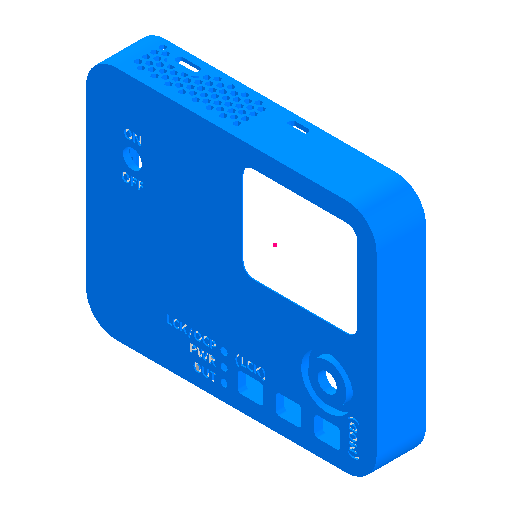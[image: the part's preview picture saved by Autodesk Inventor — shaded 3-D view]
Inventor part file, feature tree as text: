
AUTODESK INVENTOR PART (.ipt)
format: ipt  version: 2025 (Build 290162000, 162)  size: 3,334,144 bytes
history: native  units: mm
features: reference x98, sketch x43, extrude x31, other x19, fillet x6, chamfer x6, plane x4, sweep x2, mirror x2, shell x1, emboss x1, projected_geometry x1
ambient origin geometry x8: Origin, YZ Plane, XZ Plane, XY Plane, X Axis, Y Axis, Z Axis, Center Point
bodies: Solid1 (feature_tree)
feature tree (214):
  extrude  "Extrusion1"  Depth=3.0mm
  fillet  "Fillet1"  Radius=3.0mm
  shell  "Shell1"  Thickness=11.0mm
  extrude  "Extrusion_toggle"  Depth=0.3mm
  extrude  "Extrusion_encoder"  Depth=0.5mm
  extrude  "Extrusion_encoder_knob"  Depth=14.0mm
  extrude  "Extrusion_UI_BTNS"  Depth=2.6mm TaperAngle=0.0deg
  extrude  "Extrusion_Display"  Depth=2.0mm TaperAngle=0.0deg
  extrude  "Extrusion10"  Depth=10.0mm TaperAngle=0.0deg
  extrude  "Extrusion11"  Depth=3.3mm
  fillet  "Fillet4"  Radius=0.9mm
  plane  "Work Plane7"
  plane  "Work Plane8"
  extrude  "Extrusion17"  Depth=5.0mm
  extrude  "Extrusion18"  Depth=2.7mm TaperAngle=0.0deg
  sketch  "Sketch24"  dims[d107=0.25mm d108=0.0mm d109=0.3mm]
  extrude  "Extrusion19"  Depth=2.0mm
  extrude  "Extrusion20"  Depth=1.2mm
  extrude  "USB_C_1"  Depth=1.5mm TaperAngle=0.0deg
  extrude  "USB_C_2"  Depth=2.0mm TaperAngle=0.0deg
  extrude  "USB_Micro_B_1"  Depth=0.3mm
  extrude  "USB_Micro_B_2"  Depth=1.4mm TaperAngle=0.0deg
  extrude  "Venting_1"  Depth=0.25mm
  extrude  "Venting_2"  Depth=1.8mm TaperAngle=0.0deg
  sketch  "Sketch34"  dims[d142=40.0mm d144=3.0mm d145=10.0mm d147=10.0mm]
  extrude  "Extrusion27"  Depth=0.25mm
  chamfer  "Chamfer1"  Distance=1.4mm
  extrude  "Extrusion28"  Depth=7.0mm
  extrude  "Extrusion29"  TaperAngle=150.0deg  [1 undecoded]
  chamfer  "Chamfer3"  Distance=10.0mm
  extrude  "Extrusion30"  Depth=3.5mm
  extrude  "Display_hole_1"  Depth=0.3mm TaperAngle=45.0deg
  extrude  "Display_hole_2"  Depth=1.0mm
  fillet  "Fillet5"  Radius=1.0mm
  plane  "Work Plane9"
  plane  "Work Plane11"
  extrude  "Extrusion33"  Depth=0.7mm
  sweep  "Sweep2"
  chamfer  "Chamfer5"  Distance=1.8mm
  extrude  "Extrusion34"  Depth=0.7mm
  fillet  "Fillet7"  Radius=0.7mm
  chamfer  "Chamfer7"  Distance=2.5mm
  mirror  "Mirror1"
  mirror  "Mirror2"
  fillet  "Fillet8"  Radius=1.0mm
  chamfer  "Chamfer8"  Distance=1.8mm
  sketch  "Sketch44"  dims[d197=4.0mm d198=0.7mm d199=3.75mm d200=0.0mm d201=1.0mm d202=1.0mm]
  fillet  "Fillet9"  Radius=1.5mm
  sweep  "Sweep3"
  extrude  "Extrusion36"  Depth=0.4mm
  extrude  "Extrusion37"  Depth=0.4mm
  emboss  "Emboss1"
  extrude  "Extrusion38"  Depth=0.4mm
  chamfer  "Chamfer9"  Distance=4.0mm
  extrude  "Extrusion39"  Depth=0.4mm
  extrude  "Extrusion40"  Depth=0.4mm TaperAngle=0.0deg
  sketch  "Sketch1"  dims[d0=16.0mm d1=0.0mm d5=3.0mm d6=3.0mm d7=11.0mm]
  reference  "Reference1"
  reference  "Reference2"
  reference  "Reference3"
  reference  "Reference4"
  sketch  "Sketch3"  dims[d20=16.0mm d21=0.0mm d22=0.5mm]
  reference  "Reference53"
  sketch  "Sketch4"  dims[d23=16.0mm d24=0.0mm d25=14.0mm]
  reference  "Reference54"
  sketch  "Sketch5"  dims[d29=2.6mm d36=2.0mm d37=0.0mm]
  sketch  "Sketch6"  dims[d56=7.5mm d57=3.3mm d58=0.9mm]
  reference  "Reference55"
  reference  "Reference56"
  reference  "Reference57"
  reference  "Reference58"
  reference  "Reference59"
  reference  "Reference60"
  sketch  "Sketch7"  dims[d64=19.05mm d65=2.7mm d66=0.0mm]
  reference  "Reference61"
  reference  "Reference62"
  reference  "Reference63"
  reference  "Reference64"
  reference  "Reference65"
  reference  "Reference66"
  reference  "Reference67"
  reference  "Reference68"
  sketch  "Sketch10"  dims[d67=4.0mm d68=2.0mm]
  sketch  "Sketch11"  dims[d73=10.0mm d74=0.0mm d75=1.2mm]
  reference  "Reference69"
  reference  "Reference70"
  reference  "Reference71"
  sketch  "Sketch21"  dims[d101=0.5mm d102=1.5mm d103=0.0mm]
  reference  "Reference75"
  reference  "Reference76"
  reference  "Reference77"
  reference  "Reference78"
  reference  "Reference79"
  reference  "Reference80"
  reference  "Reference81"
  reference  "Reference82"
  sketch  "Sketch22"  dims[d104=1.2mm d105=2.0mm d106=0.0mm]
  reference  "Reference83"
  reference  "Reference84"
  reference  "Reference85"
  sketch  "Sketch25"  dims[d110=0.3mm d111=1.4mm d112=0.0mm]
  sketch  "Sketch26"  dims[d113=1.4mm d114=0.0mm d115=0.25mm]
  reference  "Reference86"
  reference  "Reference87"
  sketch  "Sketch27"  dims[d116=10.0mm d117=1.8mm d118=0.0mm]
  reference  "Reference88"
  reference  "Reference89"
  reference  "Reference90"
  reference  "Reference91"
  reference  "Reference92"
  reference  "Reference93"
  reference  "Reference94"
  reference  "Reference95"
  reference  "Reference96"
  sketch  "Sketch28"  dims[d119=1.8mm d120=0.0mm d121=0.25mm]
  reference  "Reference97"
  reference  "Reference98"
  reference  "Reference99"
  sketch  "Sketch29"  dims[d122=6.0mm d123=1.4mm d124=0.0mm]
  reference  "Reference100"
  reference  "Reference101"
  reference  "Reference102"
  reference  "Reference103"
  reference  "Reference104"
  reference  "Reference105"
  reference  "Reference106"
  reference  "Reference107"
  reference  "Reference108"
  reference  "Reference109"
  reference  "Reference110"
  reference  "Reference111"
  reference  "Reference112"
  reference  "Reference113"
  reference  "Reference114"
  reference  "Reference115"
  reference  "Reference116"
  reference  "Reference117"
  reference  "Reference118"
  sketch  "Sketch30"  dims[d126=3.4mm d127=7.0mm]
  reference  "Reference119"
  reference  "Reference120"
  reference  "Reference121"
  reference  "Reference122"
  sketch  "Sketch31"  dims[d136=1.4mm d137=0.0mm d138=150.0deg]
  reference  "Reference123"
  sketch  "Sketch Rectangular Pattern2"  dims[d8=3.0mm d19=0.3mm]
  sketch  "Sketch Rectangular Pattern4"  dims[d26=19.0mm d27=2.6mm d28=0.0mm]
  sketch  "Sketch33"  dims[d139=60.0deg]
  sketch  "Sketch Rectangular Pattern5"  dims[d41=10.0mm d42=10.0mm d43=0.0mm]
  sketch  "Sketch Rectangular Pattern6"  dims[d59=20.0mm d60=5.0mm]
  sketch  "Sketch35"  dims[d157=20.0mm d159=3.0mm d160=100.0mm d162=5.0mm]
  sketch  "Sketch36"  dims[d166=30.0deg]
  sketch  "Sketch37"  dims[d169=3.4mm]
  sketch  "Sketch38"  dims[d170=40.0mm d172=3.0mm d173=10.0mm d175=10.0mm]
  sketch  "Sketch39"  dims[d177=20.0mm d179=3.0mm d180=90.0mm d182=5.0mm]
  sketch  "Sketch40"  dims[d185=3.8mm]
  sketch  "Sketch41"  dims[d186=2.0mm d187=10.0mm d188=0.0mm]
  sketch  "Sketch42"  dims[d189=4.0mm d190=3.5mm]
  reference  "Reference124"
  reference  "Reference125"
  reference  "Reference126"
  projected_geometry  "Projected Loop1"
  sketch  "3D Sketch2"
  reference  "Reference127"
  reference  "Reference128"
  sketch  "Sketch43"  dims[d191=2.15mm d192=0.0mm d193=0.3mm d194=2.0mm d195=45.0deg]
  sketch  "Sketch46"  dims[d203=4.0mm d204=0.7mm]
  reference  "Reference129"
  reference  "Reference130"
  reference  "Reference131"
  reference  "Reference132"
  reference  "Reference133"
  reference  "Reference134"
  reference  "Reference135"
  reference  "Reference136"
  reference  "Reference137"
  reference  "Reference138"
  reference  "Reference139"
  reference  "Reference140"
  sketch  "Sketch47"  dims[d208=2.0mm d209=2.0mm]
  reference  "Reference141"
  reference  "Reference142"
  reference  "Reference143"
  reference  "Reference144"
  reference  "Reference145"
  reference  "Reference146"
  reference  "Reference147"
  sketch  "Sketch48"  dims[d210=2.0mm d211=1.8mm d212=0.0mm]
  sketch  "Sketch49"  dims[d213=0.3mm d214=2.0mm d215=45.0deg d216=0.7mm d217=0.7mm]
  sketch  "Sketch50"  dims[d218=0.7mm d219=2.5mm d220=0.0mm d221=1.0mm]
  reference  "Reference148"
  sketch  "3D Sketch3"
  sketch  "Sketch51"  dims[d223=2.0mm]
  sketch  "Sketch52"  dims[d225=2.0mm d229=1.8mm d230=0.0mm d231=1.5mm d233=0.8mm d234=0.0mm d238=2.0mm d241=38.0mm d242=4.0mm d243=4.0mm d244=1.8mm d245=1.0mm d246=0.0mm d249=0.05mm d250=0.0mm d251=0.0mm d252=0.2mm d253=2.0mm d254=45.0deg d255=0.23mm d256=0.23mm d257=20.071286mm d258=1.5mm d261=0.8mm d262=8.0mm d263=0.0mm d264=0.4mm d268=2.0mm d269=2.0mm d270=2.0mm d271=45.0deg d272=1.0mm d273=0.35mm d274=2.0mm d275=60.0deg d276=0.1mm d277=0.2mm d278=7.0mm d279=11.0mm d280=4.0mm d281=11.0mm d285=4.0mm d286=3.0mm d287=3.0mm d288=3.0mm d290=4.0mm d301=6.0mm d302=0.0mm d303=0.15mm d304=1.8mm d305=0.0mm d306=10.0mm d310=1.085026mm d311=2.0mm d314=2.004307mm d315=0.6mm d316=0.0mm d317=0.25mm d319=0.3mm d320=9.0mm d321=1.4mm d322=0.0mm d323=0.3mm d324=6.981317mm d325=6.981317mm d326=0.0mm d327=0.0mm d328=0.4mm d329=2.0mm d330=45.0deg d331=2.9mm d334=1.2mm d335=0.0mm d336=11.0mm d337=22.0mm d338=0.1mm d339=2.0mm d340=2.0mm d341=0.0mm d342=8.174105mm d343=6.315728mm d344=11.305971mm d345=8.672mm d346=9.928mm d347=18.531031mm d348=1.0mm d349=0.3mm d351=3.080348mm d352=1.0mm d353=3.843675mm d354=3.3mm d355=13.2mm d356=3.08mm d332=0.5mm d333=0.872665mm]
  reference  "Reference149"
  other  "USB_C_PD_PPS_sink_with_enclosure.iam"
  other  "USB_C_PD_PPS_sink:1"
  other  "USB_C_PD_PPS_sink_BOARD:1"
  other  "1M41T1B5M1QE_1M41T1B5M1QE-1:1"
  other  "FP-PEC12R-4125F-S0012-MFG_CMP-07421-000016-1:1"
  other  "B3F-1052_B3F-1052-1:2"
  other  "B3F-1052_B3F-1052-1:1"
  other  "B3F-1052_B3F-1052-1:3"
  other  "VLP-600-F_VLP-600-F-1:2"
  other  "VLP-600-F_VLP-600-F-1:3"
  other  "VLP-600-F_VLP-600-F-1:1"
  other  "3461AS_3461AS-1:2"
  other  "3461AS_3461AS-1:1"
  other  "bottom_enclosure:1"
  other  "FP-USB4085-GF-A-MFG_USB4085-GF-A-1:1"
  other  "USB-MICRO-B_V_CMP-2000-05827-1:1"
  other  "display_cover_2:1"
  other  "Button cap:1"
  other  "Button cap:3"
note: 1 required parameter value undecoded (feature->parameter linkage not recoverable at this tier; creation-order binding heuristic only, values carry confidence <= 0.55)
